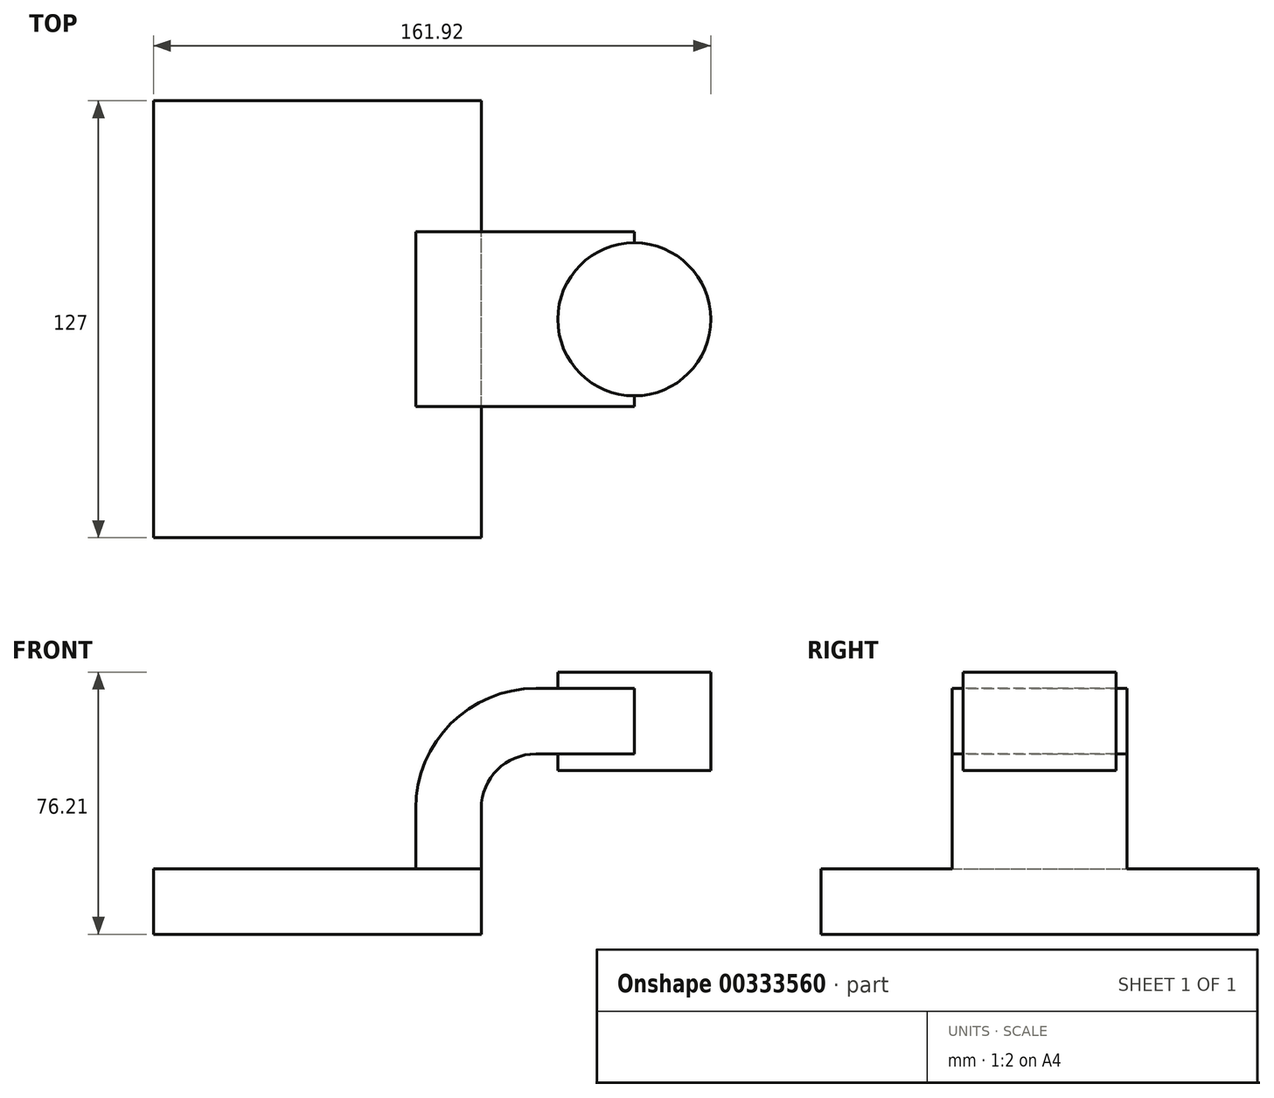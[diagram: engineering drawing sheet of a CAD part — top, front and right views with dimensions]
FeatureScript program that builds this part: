
annotation { "Feature Type Name" : "Feature", "Feature Type Description" : "" }
export const myFeature = defineFeature(function(context is Context, id is Id, definition is map)
    precondition{}
    {
        {
            var Q0;
            Q0=qCreatedBy(makeId("Front.planeOp"),FACE);
            var sketch = newSketch(context, id + "F0", { "sketchPlane" : qUnion([Q0])});
            skLineSegment(sketch, "E0.bottom", {"start": v(-47.62, -9.52) * mm, "end": v(47.63, -9.52) * mm});
            skLineSegment(sketch, "E0.top", {"start": v(-47.62, 9.53) * mm, "end": v(47.63, 9.53) * mm});
            skLineSegment(sketch, "E0.left", {"start": v(-47.63, -9.52) * mm, "end": v(-47.63, 9.53) * mm});
            skLineSegment(sketch, "E0.right", {"start": v(47.63, -9.52) * mm, "end": v(47.63, 9.53) * mm});
            skPoint(sketch, "E0.middle", {"position": v(0, 0) * mm});
            skLineSegment(sketch, "E1.bottom", {"start": v(63.5, 38.1) * mm, "end": v(114.3, 38.1) * mm});
            skLineSegment(sketch, "E1.top", {"start": v(63.5, 66.68) * mm, "end": v(114.3, 66.68) * mm});
            skLineSegment(sketch, "E1.left", {"start": v(63.5, 38.1) * mm, "end": v(63.5, 66.68) * mm});
            skLineSegment(sketch, "E1.right", {"start": v(114.3, 38.1) * mm, "end": v(114.3, 66.68) * mm});
            skPoint(sketch, "E1.middle", {"position": v(88.9, 52.39) * mm});
            skLineSegment(sketch, "E2", {"start": v(47.63, 9.53) * mm, "end": v(47.63, 27) * mm});
            skArc(sketch, "E3", {"start": v(47.62, 27) * mm, "mid": v(52.27, 38.23) * mm, "end": v(63.5, 42.88) * mm});
            skLineSegment(sketch, "E4", {"start": v(63.5, 42.88) * mm, "end": v(92.08, 42.88) * mm});
            skLineSegment(sketch, "E5.0", {"start": v(63.5, 61.93) * mm, "end": v(92.08, 61.93) * mm});
            skArc(sketch, "E5.1", {"start": v(28.58, 27) * mm, "mid": v(38.8, 51.7) * mm, "end": v(63.5, 61.93) * mm});
            skLineSegment(sketch, "E5.2", {"start": v(28.57, 9.53) * mm, "end": v(28.57, 27) * mm});
            skLineSegment(sketch, "E6", {"start": v(92.08, 38.1) * mm, "end": v(92.08, 66.68) * mm});
            skPoint(sketch, "E6.endSnap0", {"position": v(88.9, 66.68) * mm});
            skFitSpline(sketch, "E7", {"points": [v(-47.63, 9.53) * mm, v(63.5, 66.68) * mm], "startDerivative": vector(17.24, 89.4) * mm, "endDerivative": vector(149.31, 16.38) * mm});
            skSolve(sketch);
        }
        {
            var Q0;
            Q0=makeQuery(id+"F0.imprint","IMPRINT",FACE,{"disambiguationData":[TD([[makeQuery(id+"F0.imprint","IMPRINT",EDGE,{"derivedFrom":sQuery(id+"F0.wireOp",EDGE,"E0.bottom")}),1.0]])]});
            extrude(context, id + "F1", {"entities" : qUnion([Q0]), "endBound" : BoundingType.SYMMETRIC, "depth" : 127 * mm});
        }
        {
            var Q0;
            {var subQ1=sQuery(id+"F0.wireOp",EDGE,"E2");Q0=makeQuery(id+"F0.imprint","IMPRINT",FACE,{"disambiguationData":[TD([[makeQuery(id+"F0.imprint","IMPRINT",EDGE,{"derivedFrom":subQ1}),1.0]])]});}
            var Q1;
            {var subQ0=sQuery(id+"F0.wireOp",EDGE,"E4");Q1=makeQuery(id+"F0.imprint","IMPRINT",FACE,{"disambiguationData":[TD([[makeQuery(id+"F0.imprint","IMPRINT",EDGE,{"derivedFrom":subQ0}),1.0]])]});}
            extrude(context, id + "F2", {"entities" : qUnion([Q0, Q1]), "operationType" : NewBodyOperationType.ADD, "endBound" : BoundingType.SYMMETRIC, "depth" : 50.8 * mm});
        }
        {
            var Q0;
            {var subQ1=sQuery(id+"F0.wireOp",EDGE,"E5.1");Q0=makeQuery(id+"F0.imprint","IMPRINT",FACE,{"disambiguationData":[TD([[makeQuery(id+"F0.imprint","IMPRINT",EDGE,{"derivedFrom":subQ1}),1.0]])]});}
            extrude(context, id + "F3", {"entities" : qUnion([Q0]), "operationType" : NewBodyOperationType.ADD, "endBound" : BoundingType.SYMMETRIC, "depth" : 15.88 * mm});
        }
        {
            var Q0;
            {var subQ4=sQuery(id+"F0.wireOp",EDGE,"E1.right");Q0=makeQuery(id+"F0.imprint","IMPRINT",FACE,{"disambiguationData":[TD([[makeQuery(id+"F0.imprint","IMPRINT",EDGE,{"derivedFrom":subQ4}),1.0]])]});}
            var Q1;
            Q1=sQuery(id+"F0.wireOp",EDGE,"E6");
            revolve(context, id + "F4", {"operationType" : NewBodyOperationType.ADD, "entities" : qUnion([Q0]), "axis" : qUnion([Q1]), "revolveType" : RevolveType.FULL});
        }
    });
